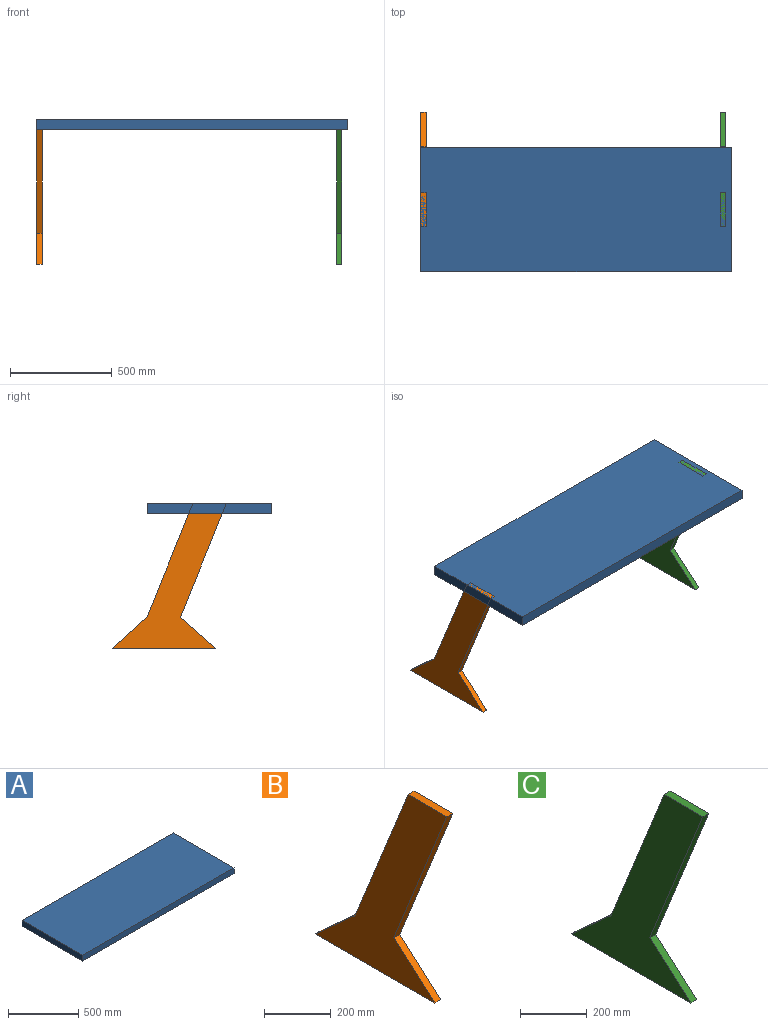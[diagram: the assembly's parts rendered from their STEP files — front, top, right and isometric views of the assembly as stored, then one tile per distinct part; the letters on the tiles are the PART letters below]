
ASSEMBLY  parts=3 mates=2
PART A: 6 faces, bbox 1524x609.6x50.8 mm
  f0: plane 1524x50.8mm, normal (0,-1,0), area 77419.2mm2, adj f1,f3,f4,f5
  f1: plane 609.6x50.8mm, normal (1,0,0), area 30967.7mm2, adj f0,f2,f4,f5
  f2: plane 1524x50.8mm, normal (0,1,0), area 77419.2mm2, adj f1,f3,f4,f5
  f3: plane 609.6x50.8mm, normal (-1,0,0), area 30967.7mm2, adj f0,f2,f4,f5
  f4: plane 1524x609.6mm, normal (0,0,-1), area 929030.4mm2, adj f0,f1,f2,f3
  f5: plane 1524x609.6mm, normal (0,0,1), area 929030.4mm2, adj f0,f1,f2,f3
PART B: 8 faces, bbox 25.4x559.6x711.2 mm
  f0: plane 164.36x25.4mm, normal (0,0,1), area 4174.9mm2, adj f1,f5,f6,f7
  f1: plane 558.61x225.65mm, normal (0,-0.93,-0.37), area 15302.6mm2, adj f0,f2,f6,f7
  f2: plane 174.02x152.59mm, normal (0,-0.66,0.75), area 5878.7mm2, adj f1,f3,f6,f7
  f3: plane 508x25.4mm, normal (0,0,-1), area 12903.2mm2, adj f2,f4,f6,f7
  f4: plane 169.61x152.59mm, normal (0,0.67,0.74), area 5795mm2, adj f3,f5,f6,f7
  f5: plane 558.61x225.65mm, normal (0,0.93,0.37), area 15302.6mm2, adj f0,f4,f6,f7
  f6: plane 711.2x559.63mm, normal (-1,0,0), area 143113.7mm2, adj f0,f1,f2,f3,f4,f5
  f7: plane 711.2x559.63mm, normal (1,0,0), area 143113.7mm2, adj f0,f1,f2,f3,f4,f5
PART C: 8 faces, bbox 25.4x559.6x711.2 mm
  f0: plane 164.36x25.4mm, normal (0,0,1), area 4174.9mm2, adj f1,f5,f6,f7
  f1: plane 558.61x225.65mm, normal (0,-0.93,-0.37), area 15302.6mm2, adj f0,f2,f6,f7
  f2: plane 174.02x152.59mm, normal (0,-0.66,0.75), area 5878.7mm2, adj f1,f3,f6,f7
  f3: plane 508x25.4mm, normal (0,0,-1), area 12903.2mm2, adj f2,f4,f6,f7
  f4: plane 169.61x152.59mm, normal (0,0.67,0.74), area 5795mm2, adj f3,f5,f6,f7
  f5: plane 558.61x225.65mm, normal (0,0.93,0.37), area 15302.6mm2, adj f0,f4,f6,f7
  f6: plane 711.2x559.63mm, normal (-1,0,0), area 143113.7mm2, adj f0,f1,f2,f3,f4,f5
  f7: plane 711.2x559.63mm, normal (1,0,0), area 143113.7mm2, adj f0,f1,f2,f3,f4,f5
PLACE A t=(788.26,-477.58,54.93)mm
PLACE B t=(788.26,-304.94,54.93)mm
PLACE C t=(762.86,-304.94,54.93)mm
MATE fastened A.f5 <-> B.f0  axis (0,0,1) through (26.26,-172.78,54.93)mm
MATE fastened A.f5 <-> C.f0  axis (0,0,1) through (26.26,-172.78,54.93)mm
